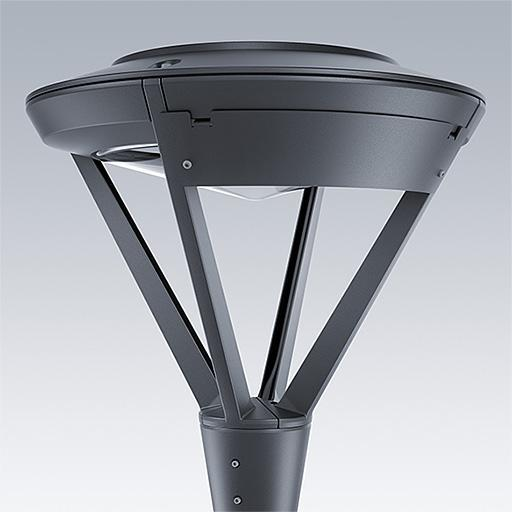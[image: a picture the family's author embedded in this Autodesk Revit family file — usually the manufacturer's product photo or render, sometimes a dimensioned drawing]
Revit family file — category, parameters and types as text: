
# Revit family: Thorn AVENUE MTP
name_source: partatom
category: Lighting Fixtures
units: mm (PartAtom-declared; Revit-internal decimal feet)

## family parameters
Always vertical = No
Cut with Voids When Loaded = Yes
Light Source = Yes
Maintain Annotation Orientation = No
Part Type = Normal
Room Calculation Point = No
Round Connector Dimension = Use Diameter
Shared = No
Work Plane-Based = No

## types (26) — shared parameters
Assembly Code = Pr_70_70_48_36
Color Filter = 16777215
Description = Roadway or street lighting luminaires
Dimming Lamp Color Temperature Shift = <None>
Export Type to IFC As = IfcLightFixtureType
External Visor = No
Is Bowl (CL/GL) = No
Lamp = LED
Light Source = 310 mm  [stored 1.01706 ft]
Manufacturer = Thorn Lighting
Material Housing = Thorn-Aluminium-RAL 7016-Anthracite Grey
SELECT ACCESSORIES = SELECT ACCESSORIES
Tilt Angle = 90.00°
Type External Visor = Thorn AVENUE Accessories : AV ext louvre ANT
Type IFC Predefined Type = DIRECTIONSOURCE
Type Image = TLG_AVEN_F_ANT_MTP60_1.jpg
URL = https://www.thornlighting.com
ZD On = No
ZU On = No
zero-valued in all types: Default Elevation

## per-type parameters (varying)
| type | Apparent Load | Model | Photometric Web File | Power Factor |
| AV 12L35-730 WSC GL CL1 WS0.3 T60 ANT | 14 VA | 96684704 | 96684704_(STD).IES | 0.97 |
| AV 12L35-730 WSC GL CL2 WS0.3 T60 ANT | 14 VA | 96684690 | 96684690_(STD).IES | 0.97 |
| AV 12L50-730 WSC GL CL1 WS0.3 T60 ANT | 20 VA | 96684705 | 96684705_(STD).IES | 0.94 |
| AV 12L50-730 WSC GL CL2 WS0.3 T60 ANT | 20 VA | 96684691 | 96684691_(STD).IES | 0.94 |
| AV 12L70-730 WSC GL CL1 WS0.3 T60 ANT | 27 VA | 96684706 | 96684706_(STD).IES | 0.97 |
| AV 12L70-730 WSC GL CL2 WS0.3 T60 ANT | 27 VA | 96684692 | 96684692_(STD).IES | 0.97 |
| AV 18L105-730 RSC GL CL1 WS0.3 T60 ANT | 61 VA | 96684711 | 96684711_(STD).IES | 0.98 |
| AV 18L105-730 RSC GL CL2 WS0.3 T60 ANT | 61 VA | 96684697 | 96684697_(STD).IES | 0.98 |
| AV 18L35-730 RSC GL CL1 WS0.3 T60 ANT | 21 VA | 96684708 | 96684708_(STD).IES | 0.94 |
| AV 18L35-730 RSC GL CL2 WS0.3 T60 ANT | 21 VA | 96684694 | 96684694_(STD).IES | 0.94 |
| AV 18L50-730 RSC GL CL1 WS0.3 T60 ANT | 29 VA | 96684709 | 96684709_(STD).IES | 0.97 |
| AV 18L50-730 RSC GL CL2 WS0.3 T60 ANT | 29 VA | 96684695 | 96684695_(STD).IES | 0.97 |
| AV 18L70-730 RSC GL CL1 WS0.3 T60 ANT | 40 VA | 96684710 | 96684710_(STD).IES | 0.98 |
| AV 18L70-730 RSC GL CL2 WS0.3 T60 ANT | 40 VA | 96684696 | 96684696_(STD).IES | 0.98 |
| AV 24L35-730 WSC GL CL1 WS0.3 T60 ANT | 28 VA | 96684712 | 96684712_(STD).IES | 0.94 |
| AV 24L35-730 WSC GL CL2 WS0.3 T60 ANT | 28 VA | 96684698 | 96684698_(STD).IES | 0.94 |
| AV 24L50-730 WSC GL CL1 WS0.3 T60 ANT | 38 VA | 96684713 | 96684713_(STD).IES | 0.97 |
| AV 24L50-730 WSC GL CL2 WS0.3 T60 ANT | 38 VA | 96684699 | 96684699_(STD).IES | 0.97 |
| AV 24L70-730 WSC GL CL1 WS0.3 T60 ANT | 53 VA | 96684714 | 96684714_(STD).IES | 0.98 |
| AV 24L70-730 WSC GL CL2 WS0.3 T60 ANT | 53 VA | 96684700 | 96684700_(STD).IES | 0.98 |
| AV 36L35-730 WSC GL CL1 WS0.3 T60 ANT | 45 VA | 96684715 | 96684715_(STD).IES | 0.86 |
| AV 36L35-730 WSC GL CL2 WS0.3 T60 ANT | 45 VA | 96684701 | 96684701_(STD).IES | 0.86 |
| AV 36L50-730 WSC GL CL1 WS0.3 T60 ANT | 59 VA | 96684716 | 96684716_(STD).IES | 0.92 |
| AV 36L50-730 WSC GL CL2 WS0.3 T60 ANT | 59 VA | 96684702 | 96684702_(STD).IES | 0.92 |
| AV 36L60-730 WSC GL CL1 WS0.3 T60 ANT | 69 VA | 96684717 | 96684717_(STD).IES | 0.94 |
| AV 36L60-730 WSC GL CL2 WS0.3 T60 ANT | 69 VA | 96684703 | 96684703_(STD).IES | 0.94 |

note: [stored X ft] marks values corroborated as IEEE doubles in the binary element streams (Revit-internal decimal feet)

## geometry (parser evidence)
native form markers: Sweep x10
no freeform markers — native parametric forms only
